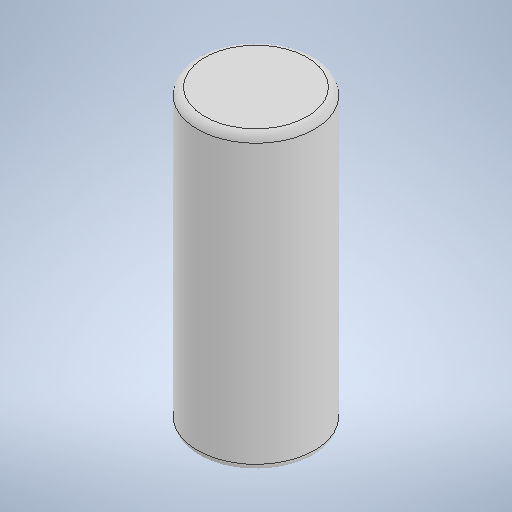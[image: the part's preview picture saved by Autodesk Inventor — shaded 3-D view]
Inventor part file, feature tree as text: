
AUTODESK INVENTOR PART (.ipt)
format: ipt  version: 2025.1 (Build 291241000, 241)  size: 266,240 bytes
history: native  units: mm
features: extrude x1, fillet x1, sketch x1
ambient origin geometry x8: Origin, YZ Plane, XZ Plane, XY Plane, X Axis, Y Axis, Z Axis, Center Point
bodies: Solid1 (feature_tree)
feature tree (3):
  extrude  "Extrusion1"  Depth=10.0mm TaperAngle=0.0deg
  fillet  "Fillet1"  Radius=0.25mm
  sketch  "Sketch1"  dims[d0=4.0mm d1=10.0mm d2=0.0mm d3=0.25mm]
